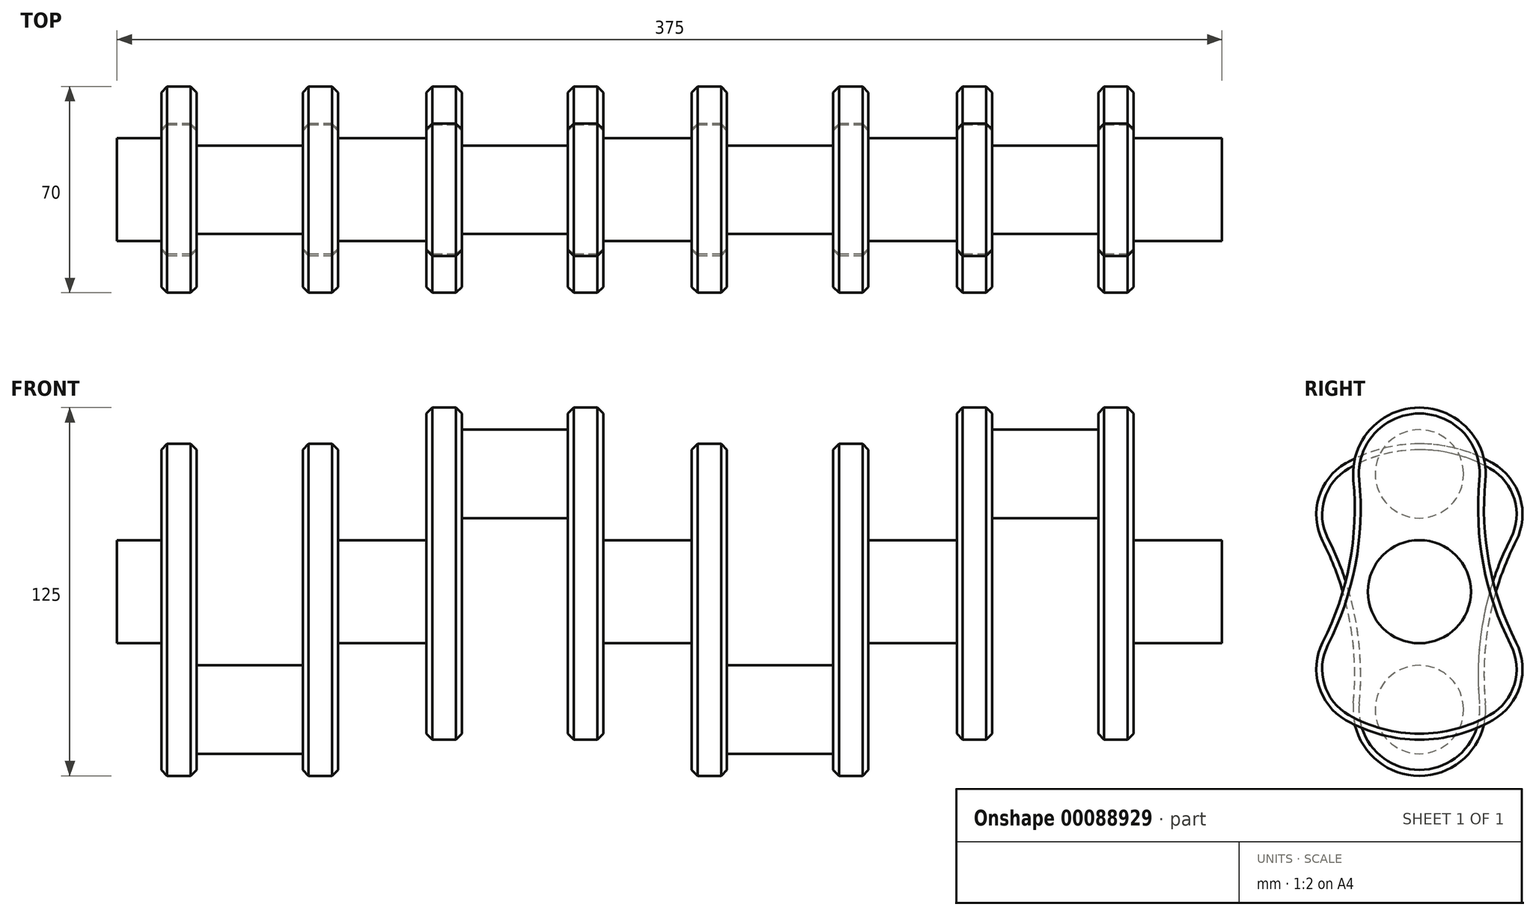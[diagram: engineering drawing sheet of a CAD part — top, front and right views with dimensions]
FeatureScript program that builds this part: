
annotation { "Feature Type Name" : "Feature", "Feature Type Description" : "" }
export const myFeature = defineFeature(function(context is Context, id is Id, definition is map)
    precondition{}
    {
        {
            var Q0;
            Q0=qCreatedBy(makeId("Right.planeOp"),FACE);
            var sketch = newSketch(context, id + "F0", { "sketchPlane" : qUnion([Q0])});
            skCircle(sketch, "E0", {"center": v(0, 0) * mm, "radius": 17.5 * mm});
            skSolve(sketch);
        }
        {
            var Q0;
            Q0=makeQuery(id+"F0.imprint","IMPRINT",FACE,{"disambiguationData":[TD([[makeQuery(id+"F0.imprint","IMPRINT",EDGE,{"derivedFrom":sQuery(id+"F0.wireOp",EDGE,"E0")}),1.0]])]});
            extrude(context, id + "F1", {"entities" : qUnion([Q0]), "depth" : 15 * mm});
        }
        {
            var Q0;
            Q0=makeQuery(id+"F1.opExtrude","CAP_FACE",FACE,{"disambiguationData":[OSD([sQuery(id+"F0.wireOp",EDGE,"E0")])],"isStart":false});
            var sketch = newSketch(context, id + "F2", { "sketchPlane" : qUnion([Q0])});
            skLineSegment(sketch, "E1", {"start": v(0, 50.2) * mm, "end": v(0, -62.5) * mm, "construction": true});
            skArc(sketch, "E2", {"start": v(0, -62.5) * mm, "mid": v(16.66, -55.12) * mm, "end": v(22.4, -37.83) * mm});
            skArc(sketch, "E3", {"start": v(32.82, 17.17) * mm, "mid": v(34.16, 31.97) * mm, "end": v(24.92, 43.61) * mm});
            skArc(sketch, "E4", {"start": v(32.82, 17.17) * mm, "mid": v(23.68, -9.59) * mm, "end": v(22.4, -37.83) * mm});
            skPoint(sketch, "E4.first.point", {"position": v(32.82, 17.17) * mm});
            skPoint(sketch, "E4.second.point", {"position": v(22.4, -37.83) * mm});
            skArc(sketch, "E5.trimOffspring", {"start": v(24.92, 43.61) * mm, "mid": v(12.9, 48.54) * mm, "end": v(0, 50.2) * mm});
            skPoint(sketch, "E6.center.orphan", {"position": v(0, 0) * mm});
            skArc(sketch, "E7.MirrorCS", {"start": v(-24.92, 43.61) * mm, "mid": v(-12.9, 48.54) * mm, "end": v(0, 50.2) * mm});
            skArc(sketch, "E8.MirrorCS", {"start": v(-32.82, 17.17) * mm, "mid": v(-34.16, 31.97) * mm, "end": v(-24.92, 43.61) * mm});
            skArc(sketch, "E9.MirrorCS", {"start": v(-32.82, 17.17) * mm, "mid": v(-23.68, -9.59) * mm, "end": v(-22.4, -37.83) * mm});
            skArc(sketch, "E10.MirrorCS", {"start": v(0, -62.5) * mm, "mid": v(-16.66, -55.12) * mm, "end": v(-22.4, -37.83) * mm});
            skSolve(sketch);
        }
        {
            var Q0;
            Q0=makeQuery(id+"F2.imprint","IMPRINT",FACE,{"disambiguationData":[TD([[makeQuery(id+"F2.imprint","IMPRINT",EDGE,{"derivedFrom":sQuery(id+"F2.wireOp",EDGE,"E2")}),1.0]])]});
            var Q1;
            Q1=makeQuery(id+"F2.imprint","IMPRINT",FACE,{"disambiguationData":[TD([[makeQuery(id+"F2.imprint","IMPRINT",EDGE,{"derivedFrom":makeQuery(id+"F1.opExtrude","CAP_EDGE",EDGE,{"disambiguationData":[OSD([sQuery(id+"F0.wireOp",EDGE,"E0")])],"isStart":false})}),1.0]])]});
            extrude(context, id + "F3", {"entities" : qUnion([Q0, Q1]), "depth" : 12 * mm});
        }
        {
            var Q0;
            Q0=makeQuery(id+"F3.opExtrude","CAP_FACE",FACE,{"disambiguationData":[OSD([sQuery(id+"F2.wireOp",EDGE,"E2"),sQuery(id+"F2.wireOp",EDGE,"E3"),sQuery(id+"F2.wireOp",EDGE,"E4"),sQuery(id+"F2.wireOp",EDGE,"E5.trimOffspring"),sQuery(id+"F2.wireOp",EDGE,"E7.MirrorCS"),sQuery(id+"F2.wireOp",EDGE,"E8.MirrorCS"),sQuery(id+"F2.wireOp",EDGE,"E9.MirrorCS"),sQuery(id+"F2.wireOp",EDGE,"E10.MirrorCS")])],"isStart":false});
            var sketch = newSketch(context, id + "F4", { "sketchPlane" : qUnion([Q0])});
            skCircle(sketch, "E11", {"center": v(0, -40) * mm, "radius": 15 * mm});
            skSolve(sketch);
        }
        {
            var Q0;
            Q0=makeQuery(id+"F3.opExtrude","CAP_EDGE",EDGE,{"disambiguationData":[OSD([sQuery(id+"F2.wireOp",EDGE,"E7.MirrorCS")])],"isStart":true});
            var Q1;
            Q1=makeQuery(id+"F3.opExtrude","CAP_EDGE",EDGE,{"disambiguationData":[OSD([sQuery(id+"F2.wireOp",EDGE,"E7.MirrorCS")])],"isStart":false});
            chamfer(context, id + "F5", {"entities" : qUnion([Q0, Q1]), "width" : 2 * mm, "tangentPropagation" : true});
        }
        {
            var Q0;
            Q0=makeQuery(id+"F4.imprint","IMPRINT",FACE,{"disambiguationData":[TD([[makeQuery(id+"F4.imprint","IMPRINT",EDGE,{"derivedFrom":sQuery(id+"F4.wireOp",EDGE,"E11")}),1.0]])]});
            extrude(context, id + "F6", {"entities" : qUnion([Q0]), "depth" : 36 * mm});
        }
        {
            var Q0;
            Q0=makeQuery(id+"F3.opExtrude","SWEPT_BODY",BODY,{"disambiguationData":[OSD([sQuery(id+"F2.wireOp",EDGE,"E2"),sQuery(id+"F2.wireOp",EDGE,"E3"),sQuery(id+"F2.wireOp",EDGE,"E4"),sQuery(id+"F2.wireOp",EDGE,"E5.trimOffspring"),sQuery(id+"F2.wireOp",EDGE,"E7.MirrorCS"),sQuery(id+"F2.wireOp",EDGE,"E8.MirrorCS"),sQuery(id+"F2.wireOp",EDGE,"E9.MirrorCS"),sQuery(id+"F2.wireOp",EDGE,"E10.MirrorCS")])]});
            var Q1;
            Q1=makeQuery(id+"F6.opExtrude","CAP_FACE",FACE,{"disambiguationData":[OSD([sQuery(id+"F4.wireOp",EDGE,"E11")])],"isStart":false});
            transform(context, id + "F7", {"entities" : qUnion([Q0]), "transformType" : TransformType.TRANSLATION_DISTANCE, "transformDirection" : qUnion([Q1]), "distance" : 48 * mm, "makeCopy" : true});
        }
        {
            var Q0;
            Q0=makeQuery(id+"F7.opPattern","COPY",FACE,{"derivedFrom":makeQuery(id+"F3.opExtrude","CAP_FACE",FACE,{"disambiguationData":[OSD([sQuery(id+"F2.wireOp",EDGE,"E2"),sQuery(id+"F2.wireOp",EDGE,"E3"),sQuery(id+"F2.wireOp",EDGE,"E4"),sQuery(id+"F2.wireOp",EDGE,"E5.trimOffspring"),sQuery(id+"F2.wireOp",EDGE,"E7.MirrorCS"),sQuery(id+"F2.wireOp",EDGE,"E8.MirrorCS"),sQuery(id+"F2.wireOp",EDGE,"E9.MirrorCS"),sQuery(id+"F2.wireOp",EDGE,"E10.MirrorCS")])],"isStart":false}),"instanceName":"1"});
            var sketch = newSketch(context, id + "F8", { "sketchPlane" : qUnion([Q0])});
            skCircle(sketch, "E12", {"center": v(0, 0) * mm, "radius": 17.5 * mm});
            skSolve(sketch);
        }
        {
            var Q0;
            Q0=makeQuery(id+"F8.imprint","IMPRINT",FACE,{"disambiguationData":[TD([[makeQuery(id+"F8.imprint","IMPRINT",EDGE,{"derivedFrom":sQuery(id+"F8.wireOp",EDGE,"E12")}),1.0]])]});
            extrude(context, id + "F9", {"entities" : qUnion([Q0]), "depth" : 30 * mm});
        }
        {
            var Q0;
            Q0=makeQuery(id+"F7.opPattern","COPY",BODY,{"derivedFrom":makeQuery(id+"F3.opExtrude","SWEPT_BODY",BODY,{"disambiguationData":[OSD([sQuery(id+"F2.wireOp",EDGE,"E2"),sQuery(id+"F2.wireOp",EDGE,"E3"),sQuery(id+"F2.wireOp",EDGE,"E4"),sQuery(id+"F2.wireOp",EDGE,"E5.trimOffspring"),sQuery(id+"F2.wireOp",EDGE,"E7.MirrorCS"),sQuery(id+"F2.wireOp",EDGE,"E8.MirrorCS"),sQuery(id+"F2.wireOp",EDGE,"E9.MirrorCS"),sQuery(id+"F2.wireOp",EDGE,"E10.MirrorCS")])]}),"instanceName":"1"});
            var Q1;
            Q1=makeQuery(id+"F9.opExtrude","CAP_FACE",FACE,{"disambiguationData":[OSD([sQuery(id+"F8.wireOp",EDGE,"E12")])],"isStart":false});
            transform(context, id + "F10", {"entities" : qUnion([Q0]), "transformType" : TransformType.TRANSLATION_DISTANCE, "transformDirection" : qUnion([Q1]), "distance" : 42 * mm, "makeCopy" : true});
        }
        {
            var Q0;
            Q0=makeQuery(id+"F10.opPattern","COPY",BODY,{"derivedFrom":makeQuery(id+"F7.opPattern","COPY",BODY,{"derivedFrom":makeQuery(id+"F3.opExtrude","SWEPT_BODY",BODY,{"disambiguationData":[OSD([sQuery(id+"F2.wireOp",EDGE,"E2"),sQuery(id+"F2.wireOp",EDGE,"E3"),sQuery(id+"F2.wireOp",EDGE,"E4"),sQuery(id+"F2.wireOp",EDGE,"E5.trimOffspring"),sQuery(id+"F2.wireOp",EDGE,"E7.MirrorCS"),sQuery(id+"F2.wireOp",EDGE,"E8.MirrorCS"),sQuery(id+"F2.wireOp",EDGE,"E9.MirrorCS"),sQuery(id+"F2.wireOp",EDGE,"E10.MirrorCS")])]}),"instanceName":"1"}),"instanceName":"1"});
            var Q1;
            Q1=makeQuery(id+"F1.opExtrude","CAP_EDGE",EDGE,{"disambiguationData":[OSD([sQuery(id+"F0.wireOp",EDGE,"E0")])],"isStart":true});
            transform(context, id + "F11", {"entities" : qUnion([Q0]), "transformType" : TransformType.ROTATION, "transformAxis" : qUnion([Q1]), "angle" : 180 * degree, "makeCopy" : false});
        }
        {
            var Q0;
            Q0=makeQuery(id+"F10.opPattern","COPY",FACE,{"derivedFrom":makeQuery(id+"F7.opPattern","COPY",FACE,{"derivedFrom":makeQuery(id+"F3.opExtrude","CAP_FACE",FACE,{"disambiguationData":[OSD([sQuery(id+"F2.wireOp",EDGE,"E2"),sQuery(id+"F2.wireOp",EDGE,"E3"),sQuery(id+"F2.wireOp",EDGE,"E4"),sQuery(id+"F2.wireOp",EDGE,"E5.trimOffspring"),sQuery(id+"F2.wireOp",EDGE,"E7.MirrorCS"),sQuery(id+"F2.wireOp",EDGE,"E8.MirrorCS"),sQuery(id+"F2.wireOp",EDGE,"E9.MirrorCS"),sQuery(id+"F2.wireOp",EDGE,"E10.MirrorCS")])],"isStart":false}),"instanceName":"1"}),"instanceName":"1"});
            var sketch = newSketch(context, id + "F12", { "sketchPlane" : qUnion([Q0])});
            skCircle(sketch, "E13", {"center": v(0, 40) * mm, "radius": 15 * mm});
            skSolve(sketch);
        }
        {
            var Q0;
            Q0=makeQuery(id+"F12.imprint","IMPRINT",FACE,{"disambiguationData":[TD([[makeQuery(id+"F12.imprint","IMPRINT",EDGE,{"derivedFrom":sQuery(id+"F12.wireOp",EDGE,"E13")}),1.0]])]});
            extrude(context, id + "F13", {"entities" : qUnion([Q0]), "depth" : 36 * mm});
        }
        {
            var Q0;
            Q0=makeQuery(id+"F10.opPattern","COPY",BODY,{"derivedFrom":makeQuery(id+"F7.opPattern","COPY",BODY,{"derivedFrom":makeQuery(id+"F3.opExtrude","SWEPT_BODY",BODY,{"disambiguationData":[OSD([sQuery(id+"F2.wireOp",EDGE,"E2"),sQuery(id+"F2.wireOp",EDGE,"E3"),sQuery(id+"F2.wireOp",EDGE,"E4"),sQuery(id+"F2.wireOp",EDGE,"E5.trimOffspring"),sQuery(id+"F2.wireOp",EDGE,"E7.MirrorCS"),sQuery(id+"F2.wireOp",EDGE,"E8.MirrorCS"),sQuery(id+"F2.wireOp",EDGE,"E9.MirrorCS"),sQuery(id+"F2.wireOp",EDGE,"E10.MirrorCS")])]}),"instanceName":"1"}),"instanceName":"1"});
            var Q1;
            Q1=makeQuery(id+"F13.opExtrude","CAP_FACE",FACE,{"disambiguationData":[OSD([sQuery(id+"F12.wireOp",EDGE,"E13")])],"isStart":false});
            transform(context, id + "F14", {"entities" : qUnion([Q0]), "transformType" : TransformType.TRANSLATION_DISTANCE, "transformDirection" : qUnion([Q1]), "distance" : 48 * mm, "makeCopy" : true});
        }
        {
            var Q0;
            Q0=makeQuery(id+"F9.opExtrude","SWEPT_BODY",BODY,{"disambiguationData":[OSD([sQuery(id+"F8.wireOp",EDGE,"E12")])]});
            var Q1;
            Q1=makeQuery(id+"F14.opPattern","COPY",FACE,{"derivedFrom":makeQuery(id+"F10.opPattern","COPY",FACE,{"derivedFrom":makeQuery(id+"F7.opPattern","COPY",FACE,{"derivedFrom":makeQuery(id+"F3.opExtrude","CAP_FACE",FACE,{"disambiguationData":[OSD([sQuery(id+"F2.wireOp",EDGE,"E2"),sQuery(id+"F2.wireOp",EDGE,"E3"),sQuery(id+"F2.wireOp",EDGE,"E4"),sQuery(id+"F2.wireOp",EDGE,"E5.trimOffspring"),sQuery(id+"F2.wireOp",EDGE,"E7.MirrorCS"),sQuery(id+"F2.wireOp",EDGE,"E8.MirrorCS"),sQuery(id+"F2.wireOp",EDGE,"E9.MirrorCS"),sQuery(id+"F2.wireOp",EDGE,"E10.MirrorCS")])],"isStart":false}),"instanceName":"1"}),"instanceName":"1"}),"instanceName":"1"});
            transform(context, id + "F15", {"entities" : qUnion([Q0]), "transformType" : TransformType.TRANSLATION_DISTANCE, "transformDirection" : qUnion([Q1]), "distance" : 90 * mm, "makeCopy" : true});
        }
        {
            var Q0;
            Q0=makeQuery(id+"F3.opExtrude","SWEPT_BODY",BODY,{"disambiguationData":[OSD([sQuery(id+"F2.wireOp",EDGE,"E2"),sQuery(id+"F2.wireOp",EDGE,"E3"),sQuery(id+"F2.wireOp",EDGE,"E4"),sQuery(id+"F2.wireOp",EDGE,"E5.trimOffspring"),sQuery(id+"F2.wireOp",EDGE,"E7.MirrorCS"),sQuery(id+"F2.wireOp",EDGE,"E8.MirrorCS"),sQuery(id+"F2.wireOp",EDGE,"E9.MirrorCS"),sQuery(id+"F2.wireOp",EDGE,"E10.MirrorCS")])]});
            var Q1;
            Q1=makeQuery(id+"F6.opExtrude","SWEPT_BODY",BODY,{"disambiguationData":[OSD([sQuery(id+"F4.wireOp",EDGE,"E11")])]});
            var Q2;
            Q2=makeQuery(id+"F7.opPattern","COPY",BODY,{"derivedFrom":makeQuery(id+"F3.opExtrude","SWEPT_BODY",BODY,{"disambiguationData":[OSD([sQuery(id+"F2.wireOp",EDGE,"E2"),sQuery(id+"F2.wireOp",EDGE,"E3"),sQuery(id+"F2.wireOp",EDGE,"E4"),sQuery(id+"F2.wireOp",EDGE,"E5.trimOffspring"),sQuery(id+"F2.wireOp",EDGE,"E7.MirrorCS"),sQuery(id+"F2.wireOp",EDGE,"E8.MirrorCS"),sQuery(id+"F2.wireOp",EDGE,"E9.MirrorCS"),sQuery(id+"F2.wireOp",EDGE,"E10.MirrorCS")])]}),"instanceName":"1"});
            var Q3;
            Q3=makeQuery(id+"F9.opExtrude","SWEPT_BODY",BODY,{"disambiguationData":[OSD([sQuery(id+"F8.wireOp",EDGE,"E12")])]});
            var Q4;
            Q4=makeQuery(id+"F10.opPattern","COPY",BODY,{"derivedFrom":makeQuery(id+"F7.opPattern","COPY",BODY,{"derivedFrom":makeQuery(id+"F3.opExtrude","SWEPT_BODY",BODY,{"disambiguationData":[OSD([sQuery(id+"F2.wireOp",EDGE,"E2"),sQuery(id+"F2.wireOp",EDGE,"E3"),sQuery(id+"F2.wireOp",EDGE,"E4"),sQuery(id+"F2.wireOp",EDGE,"E5.trimOffspring"),sQuery(id+"F2.wireOp",EDGE,"E7.MirrorCS"),sQuery(id+"F2.wireOp",EDGE,"E8.MirrorCS"),sQuery(id+"F2.wireOp",EDGE,"E9.MirrorCS"),sQuery(id+"F2.wireOp",EDGE,"E10.MirrorCS")])]}),"instanceName":"1"}),"instanceName":"1"});
            var Q5;
            Q5=makeQuery(id+"F13.opExtrude","SWEPT_BODY",BODY,{"disambiguationData":[OSD([sQuery(id+"F12.wireOp",EDGE,"E13")])]});
            var Q6;
            Q6=makeQuery(id+"F14.opPattern","COPY",BODY,{"derivedFrom":makeQuery(id+"F10.opPattern","COPY",BODY,{"derivedFrom":makeQuery(id+"F7.opPattern","COPY",BODY,{"derivedFrom":makeQuery(id+"F3.opExtrude","SWEPT_BODY",BODY,{"disambiguationData":[OSD([sQuery(id+"F2.wireOp",EDGE,"E2"),sQuery(id+"F2.wireOp",EDGE,"E3"),sQuery(id+"F2.wireOp",EDGE,"E4"),sQuery(id+"F2.wireOp",EDGE,"E5.trimOffspring"),sQuery(id+"F2.wireOp",EDGE,"E7.MirrorCS"),sQuery(id+"F2.wireOp",EDGE,"E8.MirrorCS"),sQuery(id+"F2.wireOp",EDGE,"E9.MirrorCS"),sQuery(id+"F2.wireOp",EDGE,"E10.MirrorCS")])]}),"instanceName":"1"}),"instanceName":"1"}),"instanceName":"1"});
            var Q7;
            Q7=makeQuery(id+"F15.opPattern","COPY",BODY,{"derivedFrom":makeQuery(id+"F9.opExtrude","SWEPT_BODY",BODY,{"disambiguationData":[OSD([sQuery(id+"F8.wireOp",EDGE,"E12")])]}),"instanceName":"1"});
            var Q8;
            Q8=makeQuery(id+"F15.opPattern","COPY",FACE,{"derivedFrom":makeQuery(id+"F9.opExtrude","CAP_FACE",FACE,{"disambiguationData":[OSD([sQuery(id+"F8.wireOp",EDGE,"E12")])],"isStart":false}),"instanceName":"1"});
            transform(context, id + "F16", {"entities" : qUnion([Q0, Q1, Q2, Q3, Q4, Q5, Q6, Q7]), "transformType" : TransformType.TRANSLATION_DISTANCE, "transformDirection" : qUnion([Q8]), "distance" : 180 * mm, "makeCopy" : true});
        }
    });
